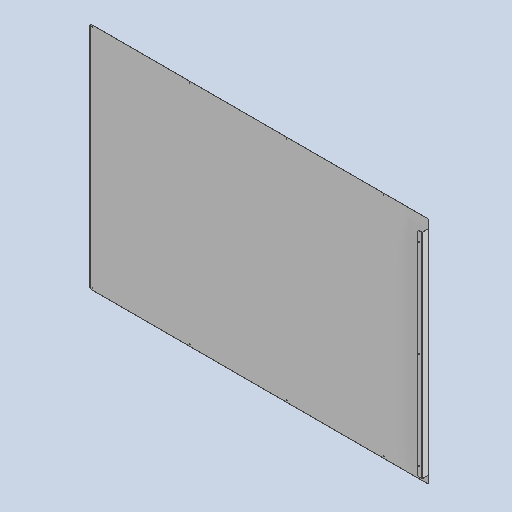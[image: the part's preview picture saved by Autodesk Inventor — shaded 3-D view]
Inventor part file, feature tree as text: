
AUTODESK INVENTOR PART (.ipt)
format: ipt  version: 2025 (Build 290162010, 162A)  size: 241,664 bytes
history: native  units: mm
features: sheet_metal_op x7, other x4, sketch x4, extrude x2, pattern_linear x2, projected_geometry x2, chamfer x1
ambient origin geometry x8: Origin, YZ Plane, XZ Plane, XY Plane, X Axis, Y Axis, Z Axis, Center Point
bodies: Solid1 (feature_tree)
feature tree (22):
  sheet_metal_op  "Face1"
  sheet_metal_op  "Flange1"
  sheet_metal_op  "Flange2"
  extrude  "Extrusion4"  Depth=1420.0mm
  pattern_linear  "Rectangular Pattern6"  Spacing1=1.6mm  [1 undecoded]
  extrude  "Extrusion5"  Depth=0.8mm
  pattern_linear  "Rectangular Pattern7"  Spacing1=41.0mm  [1 undecoded]
  chamfer  "Corner Round1"
  other  "Plate1"
  sketch  "Sketch5"  dims[d0=2095.0mm d1=1420.0mm]
  other  "Plate2"
  sheet_metal_op  "Bend1"
  sheet_metal_op  "Corner1"
  sketch  "Sketch6"  dims[d2=0.8mm]
  other  "Plate3"
  sheet_metal_op  "Bend2"
  sheet_metal_op  "Corner2"
  sketch  "Sketch8"  dims[d50=0.8mm]
  projected_geometry  "Projected Loop3"
  sketch  "Sketch9"  dims[d51=0.4mm d52=1.6mm d53=0.8mm d54=41.0mm d55=90.0deg d56=0.8mm d57=3.2mm d58=0.8mm d59=0.8mm d60=0.8mm d61=0.4mm d62=1.6mm d63=0.8mm d64=25.0mm d65=14.835299mm d66=0.8mm d67=3.2mm d68=0.8mm d69=0.8mm d80=50.0mm d81=50.0mm d82=5.0mm d83=18.0mm d84=0.8mm d85=0.0mm d86=30.0mm d88=600.0mm d89=10.0mm d90=6.0mm d91=15.0mm d92=0.8mm d93=0.0mm d94=40.0mm d96=600.0mm d97=6.0mm]
  projected_geometry  "Projected Loop4"
  other  "Definition1"
note: 2 required parameter values undecoded (feature->parameter linkage not recoverable at this tier; creation-order binding heuristic only, values carry confidence <= 0.55)
